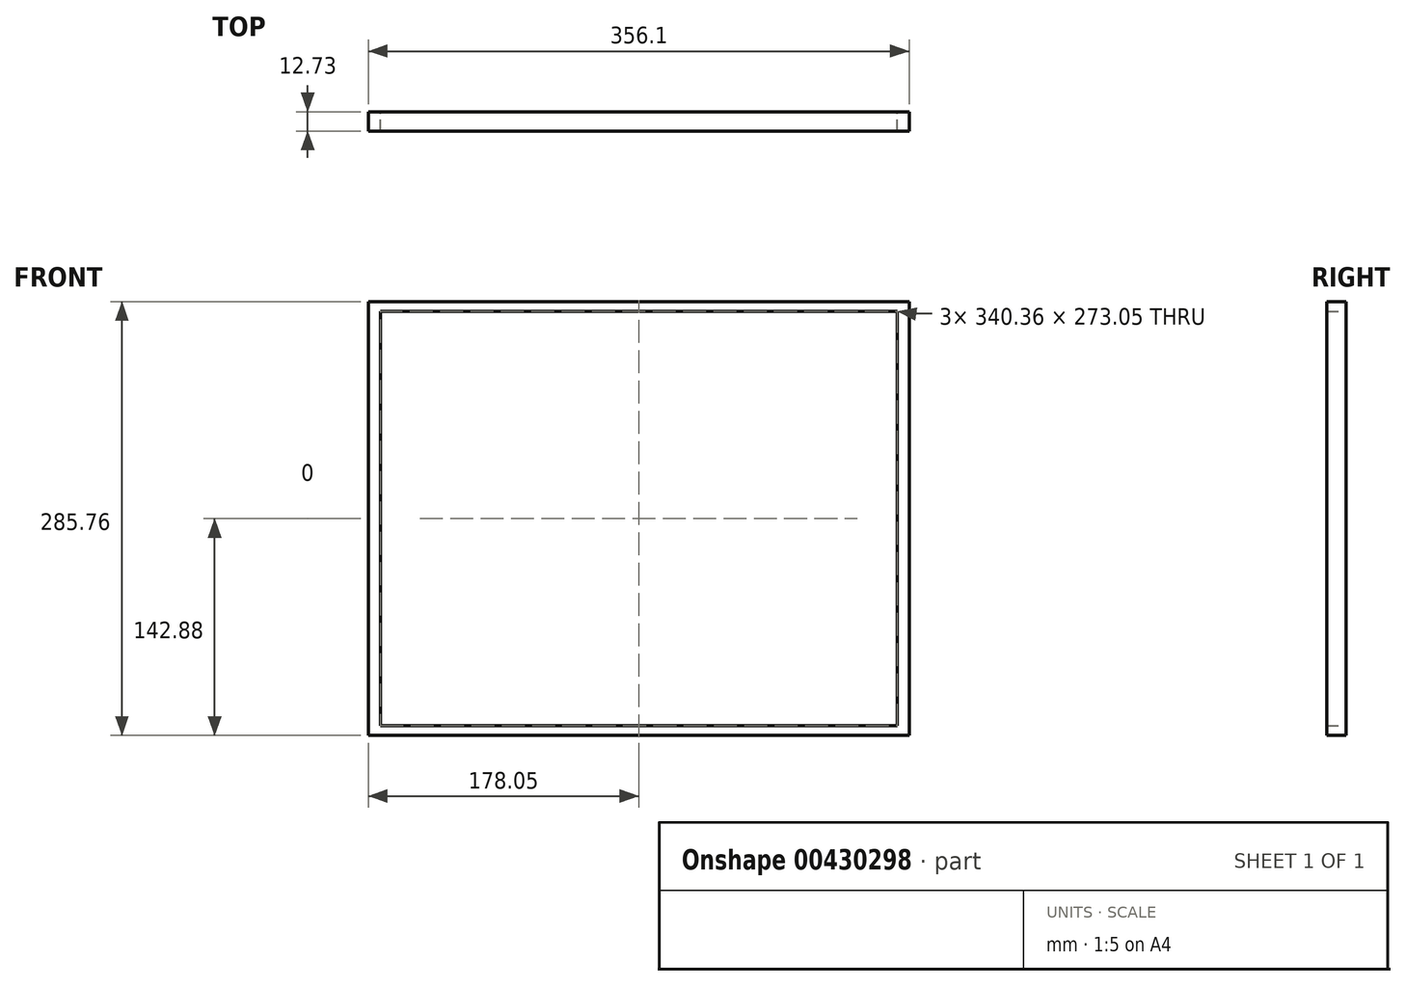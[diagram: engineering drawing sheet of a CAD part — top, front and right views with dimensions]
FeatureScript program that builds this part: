
annotation { "Feature Type Name" : "Feature", "Feature Type Description" : "" }
export const myFeature = defineFeature(function(context is Context, id is Id, definition is map)
    precondition{}
    {
        {
            var Q0;
            Q0=qCreatedBy(makeId("Front.planeOp"),FACE);
            var sketch = newSketch(context, id + "F0", { "sketchPlane" : qUnion([Q0])});
            skLineSegment(sketch, "E0.bottom", {"start": v(170.18, 136.53) * mm, "end": v(-170.18, 136.53) * mm});
            skLineSegment(sketch, "E0.top", {"start": v(170.18, -136.53) * mm, "end": v(-170.18, -136.53) * mm});
            skLineSegment(sketch, "E0.left", {"start": v(170.18, 136.53) * mm, "end": v(170.18, -136.53) * mm});
            skLineSegment(sketch, "E0.right", {"start": v(-170.18, 136.53) * mm, "end": v(-170.18, -136.53) * mm});
            skPoint(sketch, "E0.middle", {"position": v(0, 0) * mm});
            skLineSegment(sketch, "E1.0", {"start": v(178.05, -142.88) * mm, "end": v(-178.05, -142.88) * mm});
            skLineSegment(sketch, "E1.1", {"start": v(178.05, 142.88) * mm, "end": v(178.05, -142.88) * mm});
            skLineSegment(sketch, "E1.2", {"start": v(178.05, 142.88) * mm, "end": v(-178.05, 142.88) * mm});
            skLineSegment(sketch, "E1.3", {"start": v(-178.05, 142.88) * mm, "end": v(-178.05, -142.88) * mm});
            skSolve(sketch);
        }
        {
            var Q0;
            Q0=makeQuery(id+"F0.imprint","IMPRINT",FACE,{"disambiguationData":[TD([[makeQuery(id+"F0.imprint","IMPRINT",EDGE,{"derivedFrom":sQuery(id+"F0.wireOp",EDGE,"E0.bottom")}),1.0]])]});
            extrude(context, id + "F1", {"entities" : qUnion([Q0]), "depth" : 12.7 * mm});
        }
        {
            var Q0;
            Q0=makeQuery(id+"F0.imprint","IMPRINT",FACE,{"disambiguationData":[TD([[makeQuery(id+"F0.imprint","IMPRINT",EDGE,{"derivedFrom":sQuery(id+"F0.wireOp",EDGE,"E0.bottom")}),-1.0]])]});
            extrude(context, id + "F2", {"entities" : qUnion([Q0]), "depth" : 12.7 * mm});
        }
        {
            var Q0;
            Q0=makeQuery(id+"F1.opExtrude","CAP_FACE",FACE,{"disambiguationData":[OSD([sQuery(id+"F0.wireOp",EDGE,"E0.bottom"),sQuery(id+"F0.wireOp",EDGE,"E0.top"),sQuery(id+"F0.wireOp",EDGE,"E0.left"),sQuery(id+"F0.wireOp",EDGE,"E0.right")])],"isStart":true});
            var sketch = newSketch(context, id + "F3", { "sketchPlane" : qUnion([Q0])});
            skLineSegment(sketch, "E2.bottom", {"start": v(-170.18, 136.53) * mm, "end": v(170.18, 136.53) * mm});
            skLineSegment(sketch, "E2.top", {"start": v(-170.18, -136.53) * mm, "end": v(170.18, -136.53) * mm});
            skLineSegment(sketch, "E2.left", {"start": v(-170.18, 136.53) * mm, "end": v(-170.18, -136.53) * mm});
            skLineSegment(sketch, "E2.right", {"start": v(170.18, 136.53) * mm, "end": v(170.18, -136.53) * mm});
            skSolve(sketch);
        }
        {
            var Q0;
            Q0=makeQuery(id+"F3.imprint","IMPRINT",FACE,{"disambiguationData":[TD([[makeQuery(id+"F3.imprint","IMPRINT",EDGE,{"derivedFrom":sQuery(id+"F3.wireOp",EDGE,"E2.bottom")}),-1.0]])]});
            extrude(context, id + "F4", {"entities" : qUnion([Q0]), "depth" : 0.03 * mm});
        }
    });
